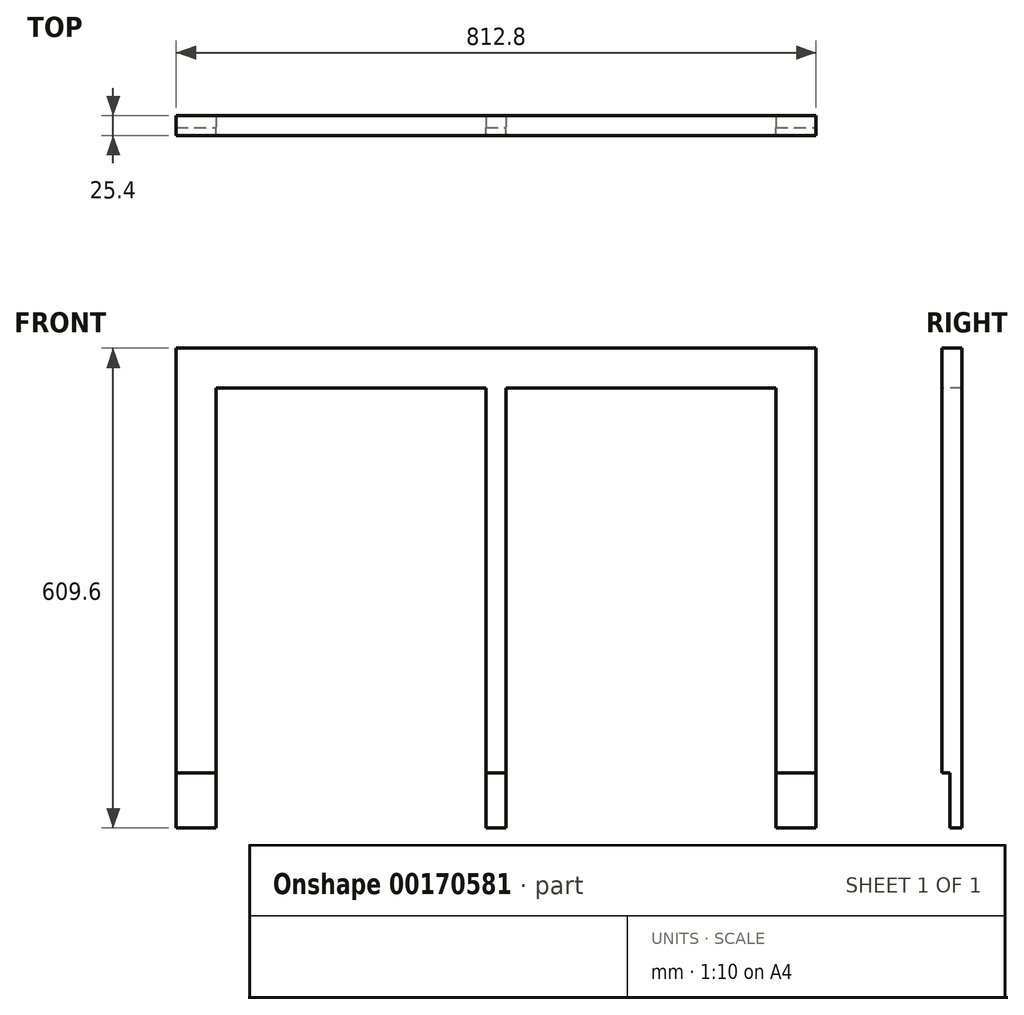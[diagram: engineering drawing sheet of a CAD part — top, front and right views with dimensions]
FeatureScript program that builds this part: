
annotation { "Feature Type Name" : "Feature", "Feature Type Description" : "" }
export const myFeature = defineFeature(function(context is Context, id is Id, definition is map)
    precondition{}
    {
        {
            var Q0;
            Q0=qCreatedBy(makeId("Right.planeOp"),FACE);
            var sketch = newSketch(context, id + "F0", { "sketchPlane" : qUnion([Q0])});
            skLineSegment(sketch, "E0.bottom", {"start": v(-10.16, 539.75) * mm, "end": v(15.24, 539.75) * mm});
            skLineSegment(sketch, "E0.top", {"start": v(-10.16, -69.85) * mm, "end": v(15.24, -69.85) * mm});
            skLineSegment(sketch, "E0.left", {"start": v(-10.16, 539.75) * mm, "end": v(-10.16, -69.85) * mm});
            skLineSegment(sketch, "E0.right", {"start": v(15.24, 539.75) * mm, "end": v(15.24, -69.85) * mm});
            skSolve(sketch);
        }
        {
            var Q0;
            Q0=makeQuery(id+"F0.imprint","IMPRINT",FACE,{"disambiguationData":[TD([[makeQuery(id+"F0.imprint","IMPRINT",EDGE,{"derivedFrom":sQuery(id+"F0.wireOp",EDGE,"E0.bottom")}),-1.0]])]});
            extrude(context, id + "F1", {"entities" : qUnion([Q0]), "endBound" : BoundingType.SYMMETRIC, "depth" : 812.8 * mm});
        }
        {
            var Q0;
            Q0=qCreatedBy(makeId("Front.planeOp"),FACE);
            var sketch = newSketch(context, id + "F2", { "sketchPlane" : qUnion([Q0])});
            skLineSegment(sketch, "E1.bottom", {"start": v(-355.6, 488.95) * mm, "end": v(-12.7, 488.95) * mm});
            skLineSegment(sketch, "E1.top", {"start": v(-355.6, -69.85) * mm, "end": v(-12.7, -69.85) * mm});
            skLineSegment(sketch, "E1.left", {"start": v(-355.6, 488.95) * mm, "end": v(-355.6, -69.85) * mm});
            skLineSegment(sketch, "E1.right", {"start": v(-12.7, 488.95) * mm, "end": v(-12.7, -69.85) * mm});
            skLineSegment(sketch, "E2", {"start": v(0, 0) * mm, "end": v(0, 605.99) * mm, "construction": true});
            skLineSegment(sketch, "E3.MirrorCS", {"start": v(355.6, -69.85) * mm, "end": v(12.7, -69.85) * mm});
            skLineSegment(sketch, "E4.MirrorCS", {"start": v(12.7, 488.95) * mm, "end": v(12.7, -69.85) * mm});
            skLineSegment(sketch, "E5.MirrorCS", {"start": v(355.6, 488.95) * mm, "end": v(12.7, 488.95) * mm});
            skLineSegment(sketch, "E6.MirrorCS", {"start": v(355.6, 488.95) * mm, "end": v(355.6, -69.85) * mm});
            skSolve(sketch);
        }
        {
            var Q0;
            Q0 = qSketchRegion(id + "F2", true);
            extrude(context, id + "F3", {"entities" : qUnion([Q0]), "operationType" : NewBodyOperationType.REMOVE, "endBound" : BoundingType.THROUGH_ALL, "oppositeDirection" : true, "depth" : 25.4 * mm, "hasSecondDirection" : true, "secondDirectionBound" : SecondDirectionBoundingType.THROUGH_ALL, "secondDirectionOppositeDirection" : false, "secondDirectionDepth" : 25.4 * mm});
        }
        {
            var Q0;
            Q0=qCreatedBy(makeId("Right.planeOp"),FACE);
            var sketch = newSketch(context, id + "F4", { "sketchPlane" : qUnion([Q0])});
            skLineSegment(sketch, "E7.bottom", {"start": v(0, -69.85) * mm, "end": v(-10.16, -69.85) * mm});
            skLineSegment(sketch, "E7.top", {"start": v(0, 0) * mm, "end": v(-10.16, 0) * mm});
            skLineSegment(sketch, "E7.left", {"start": v(0, -69.85) * mm, "end": v(0, 0) * mm});
            skLineSegment(sketch, "E7.right", {"start": v(-10.16, -69.85) * mm, "end": v(-10.16, 0) * mm});
            skSolve(sketch);
        }
        {
            var Q0;
            Q0 = qSketchRegion(id + "F4", true);
            extrude(context, id + "F5", {"entities" : qUnion([Q0]), "operationType" : NewBodyOperationType.REMOVE, "endBound" : BoundingType.THROUGH_ALL, "oppositeDirection" : true, "depth" : 25.4 * mm, "hasSecondDirection" : true, "secondDirectionBound" : SecondDirectionBoundingType.THROUGH_ALL, "secondDirectionOppositeDirection" : false, "secondDirectionDepth" : 25.4 * mm});
        }
    });
